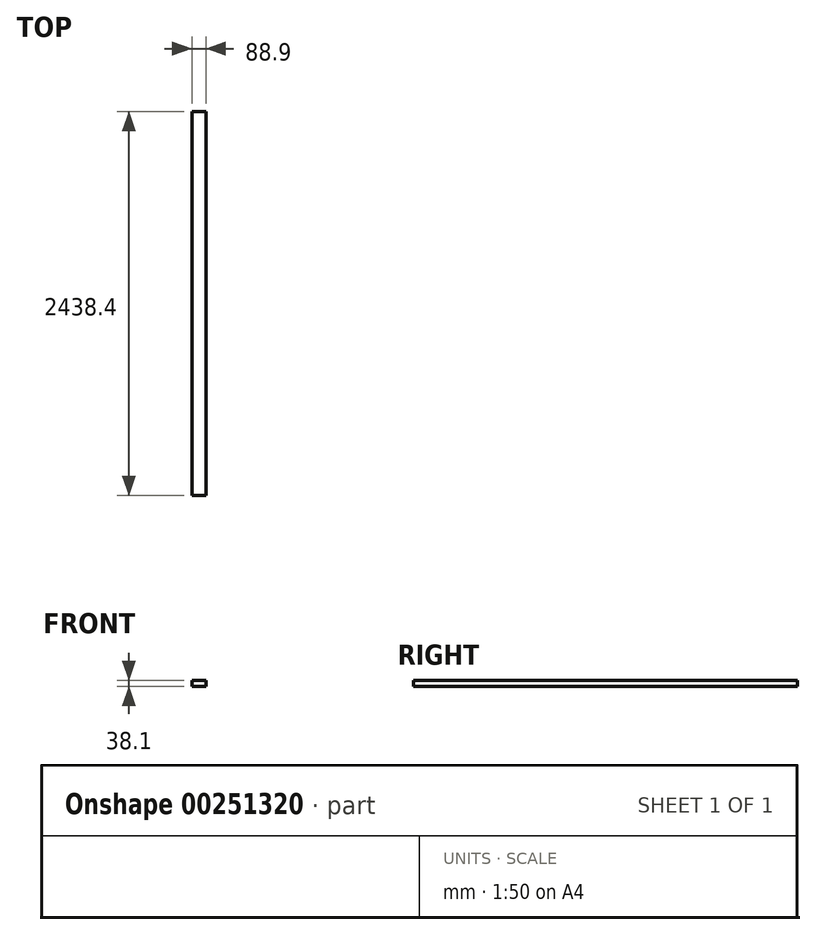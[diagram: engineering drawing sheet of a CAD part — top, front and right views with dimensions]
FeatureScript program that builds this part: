
annotation { "Feature Type Name" : "Feature", "Feature Type Description" : "" }
export const myFeature = defineFeature(function(context is Context, id is Id, definition is map)
    precondition{}
    {
        {
            var Q0;
            Q0=qCreatedBy(makeId("Top.planeOp"),FACE);
            var sketch = newSketch(context, id + "F0", { "sketchPlane" : qUnion([Q0])});
            skLineSegment(sketch, "E0.bottom", {"start": v(-75.42, 1896.16) * mm, "end": v(13.48, 1896.16) * mm});
            skLineSegment(sketch, "E0.top", {"start": v(-75.42, -542.24) * mm, "end": v(13.48, -542.24) * mm});
            skLineSegment(sketch, "E0.left", {"start": v(-75.42, 1896.16) * mm, "end": v(-75.42, -542.24) * mm});
            skLineSegment(sketch, "E0.right", {"start": v(13.48, 1896.16) * mm, "end": v(13.48, -542.24) * mm});
            skSolve(sketch);
        }
        {
            var Q0;
            Q0=makeQuery(id+"F0.imprint","IMPRINT",FACE,{"disambiguationData":[TD([[makeQuery(id+"F0.imprint","IMPRINT",EDGE,{"derivedFrom":sQuery(id+"F0.wireOp",EDGE,"E0.bottom")}),-1.0]])]});
            extrude(context, id + "F1", {"entities" : qUnion([Q0]), "depth" : 38.1 * mm});
        }
    });
